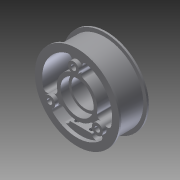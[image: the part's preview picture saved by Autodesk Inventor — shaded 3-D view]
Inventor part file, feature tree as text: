
AUTODESK INVENTOR PART (.ipt)
format: ipt  version: 2012 (Build 160160000, 160)  size: 309,760 bytes
history: native  units: in
note: dims shown in document units (in); Inventor stores cm internally (conversion verified against a paired STEP export)
features: extrude x10, thread x4, sketch x3, fillet x1
ambient origin geometry x8: Origin, YZ Plane, XZ Plane, XY Plane, X Axis, Y Axis, Z Axis, Center Point
bodies: Solid1 (feature_tree)
feature tree (18):
  sketch  "Sketch1"  dims[d0=2.875in d1=2.625in]
  extrude  "Extrusion1"  Depth=2.625in
  extrude  "Extrusion2"  Depth=0.9375in
  extrude  "Extrusion3"  Depth=0.125in
  fillet  "Fillet1"  Radius=0.1875in
  extrude  "Extrusion4"  Depth=0.6875in
  extrude  "Extrusion5"  Depth=1.1875in
  sketch  "Sketch2"  dims[d8=0.18in d10=0.9375in]
  extrude  "Extrusion8"  Depth=0.125in
  extrude  "Extrusion9"  Depth=0.1875in
  extrude  "Extrusion10"  Depth=0.9375in
  extrude  "Extrusion11"  TaperAngle=120.0deg  [1 undecoded]
  thread  "Thread1"  [1 undecoded]
  thread  "Thread2"  [1 undecoded]
  thread  "Thread3"  [1 undecoded]
  thread  "Thread4"  [1 undecoded]
  extrude  "Extrusion12"  Depth=0.9375in
  sketch  "Sketch4"  dims[d11=1.125in d12=0.125in d13=0.1875in d14=0.6875in d15=1.1875in d16=0.125in d17=0.1875in d18=0.9375in d19=120.0deg d24=1.0in d25=0.0in d26=0.9375in d27=0.0in d28=0.0625in d29=0.0in d30=0.125in d31=0.9375in d32=0.725in d33=0.0in d34=0.275in d35=0.0in d41=0.125in d42=0.0in d43=1.1811in d45=360.0deg d50=0.75in d51=0.1875in d52=0.875in d53=0.0in d54=0.125in d55=0.0in d56=0.138in d57=0.125in d58=0.125in d59=0.125in d61=0.125in d62=0.0in d63=1.0in d64=0.0in d65=1.0in d66=0.0in d67=1.0in d68=0.0in d69=1.0in d70=0.0in d72=0.125in d73=0.25in d74=0.125in d75=0.125in d76=0.125in d77=0.0in]
note: 5 required parameter values undecoded (feature->parameter linkage not recoverable at this tier; creation-order binding heuristic only, values carry confidence <= 0.55)
